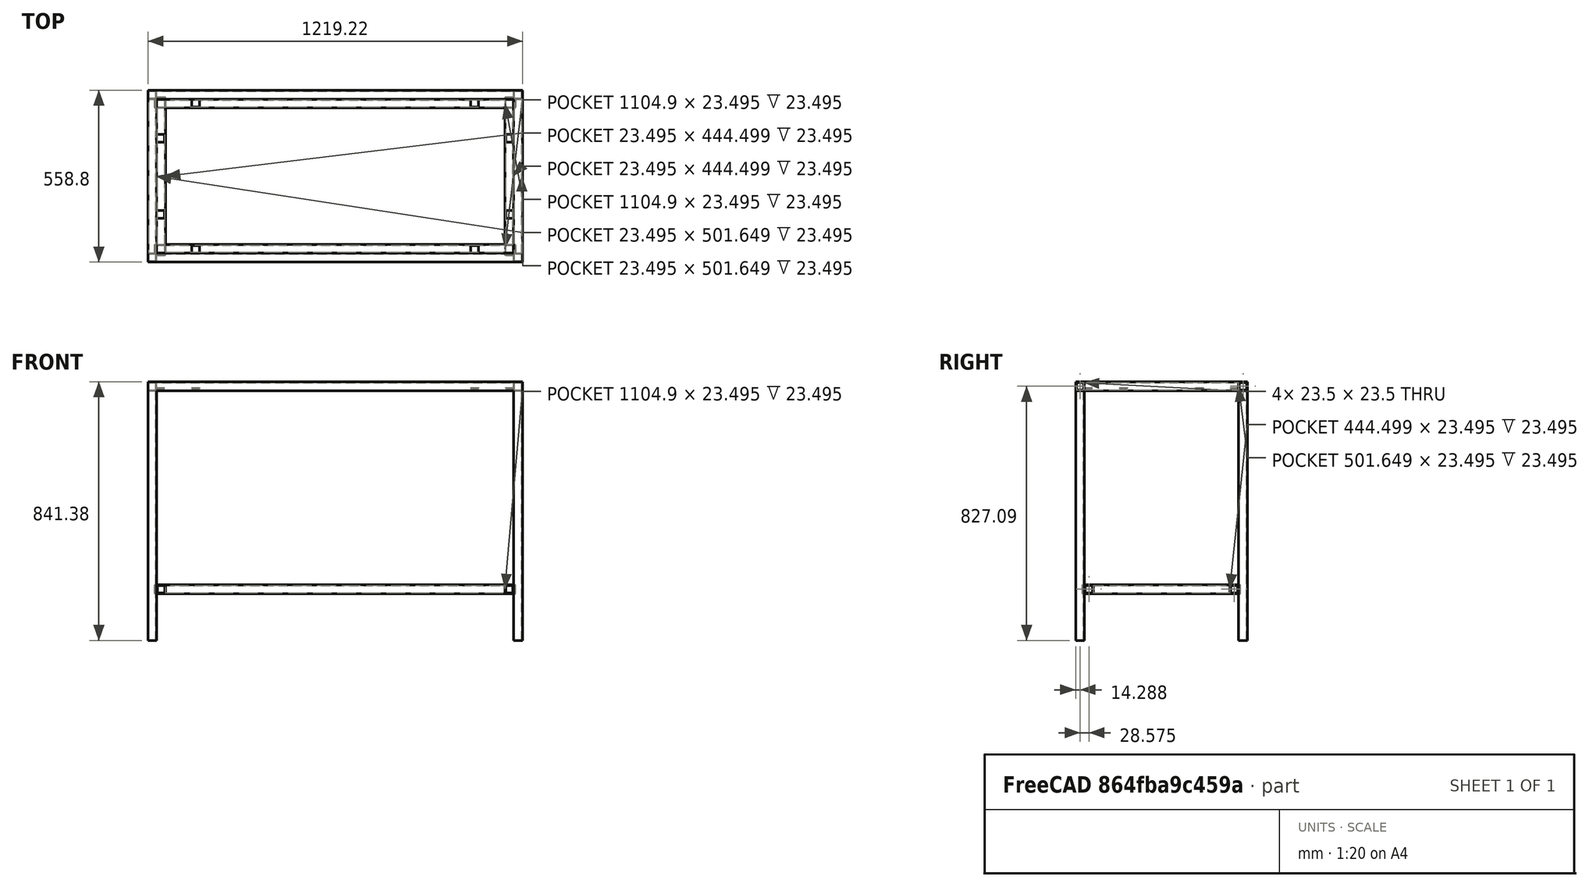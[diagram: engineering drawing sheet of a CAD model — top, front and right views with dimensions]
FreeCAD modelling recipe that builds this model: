
FCSTD DOCUMENT  (FreeCAD 0.21R33668 +26 (Git))
Label: Frame
License: All rights reserved
LicenseURL: http://en.wikipedia.org/wiki/All_rights_reserved
objects: Part::Box×32, Part::Cut×12, Part::MultiFuse×5
note: 49 computed .brp shape members not serialized (recipe doc carries the construction recipe); baked Part::Feature solids carry a one-line shape summary decoded from their .brp

FEATURE [Part::Box] cube
  AttacherType = Attacher::AttachEngine3D
  Height = 28.575
  Length = 1219.21
  Placement = pos=(-609.605,-14.2875,-14.2875) rot=(0,0,1;0rad)
  Width = 28.575
FEATURE [Part::Box] cube001
  AttacherType = Attacher::AttachEngine3D
  Height = 23.495
  Length = 1219.23
  Placement = pos=(-609.615,-11.7475,-11.7475) rot=(0,0,1;0rad)
  Width = 23.495
FEATURE [Part::Cut] difference
  Base = -> cube
  Placement = pos=(0,265.112,0) rot=(0,0,1;0rad)
  Tool = -> cube001
FEATURE [Part::Box] cube002
  AttacherType = Attacher::AttachEngine3D
  Height = 28.575
  Length = 1219.21
  Placement = pos=(-609.605,-14.2875,-14.2875) rot=(0,0,1;0rad)
  Width = 28.575
FEATURE [Part::Box] cube003
  AttacherType = Attacher::AttachEngine3D
  Height = 23.495
  Length = 1219.23
  Placement = pos=(-609.615,-11.7475,-11.7475) rot=(0,0,1;0rad)
  Width = 23.495
FEATURE [Part::Cut] difference001
  Base = -> cube002
  Placement = pos=(0,-265.112,0) rot=(0,0,1;0rad)
  Tool = -> cube003
FEATURE [Part::Box] cube004
  AttacherType = Attacher::AttachEngine3D
  Height = 28.575
  Length = 501.66
  Placement = pos=(-250.83,-14.2875,-14.2875) rot=(0,0,1;0rad)
  Width = 28.575
FEATURE [Part::Box] cube005
  AttacherType = Attacher::AttachEngine3D
  Height = 23.495
  Length = 501.68
  Placement = pos=(-250.84,-11.7475,-11.7475) rot=(0,0,1;0rad)
  Width = 23.495
FEATURE [Part::Cut] difference002
  Base = -> cube004
  Placement = pos=(595.312,0,0) rot=(0,0,1;1.5708rad)
  Tool = -> cube005
FEATURE [Part::Box] cube006
  AttacherType = Attacher::AttachEngine3D
  Height = 28.575
  Length = 501.66
  Placement = pos=(-250.83,-14.2875,-14.2875) rot=(0,0,1;0rad)
  Width = 28.575
FEATURE [Part::Box] cube007
  AttacherType = Attacher::AttachEngine3D
  Height = 23.495
  Length = 501.68
  Placement = pos=(-250.84,-11.7475,-11.7475) rot=(0,0,1;0rad)
  Width = 23.495
FEATURE [Part::Cut] difference003
  Base = -> cube006
  Placement = pos=(-595.312,0,0) rot=(0,0,1;1.5708rad)
  Tool = -> cube007
FEATURE [Part::MultiFuse] Group
  Shapes = -> [difference,difference001,difference002,difference003]
FEATURE [Part::Box] cube008
  AttacherType = Attacher::AttachEngine3D
  Height = 3.175
  Length = 25.4
  Placement = pos=(555.625,-136.525,-7.65175) rot=(0,0,1;0rad)
  Width = 25.4
FEATURE [Part::Box] cube009
  AttacherType = Attacher::AttachEngine3D
  Height = 3.175
  Length = 25.4
  Placement = pos=(555.625,111.125,-7.65175) rot=(0,0,1;0rad)
  Width = 25.4
FEATURE [Part::Box] cube010
  AttacherType = Attacher::AttachEngine3D
  Height = 3.175
  Length = 25.4
  Placement = pos=(-581.025,-136.525,-7.65175) rot=(0,0,1;0rad)
  Width = 25.4
FEATURE [Part::Box] cube011
  AttacherType = Attacher::AttachEngine3D
  Height = 3.175
  Length = 25.4
  Placement = pos=(-581.025,111.125,-7.65175) rot=(0,0,1;0rad)
  Width = 25.4
FEATURE [Part::Box] cube012
  AttacherType = Attacher::AttachEngine3D
  Height = 3.175
  Length = 25.4
  Placement = pos=(-466.725,225.425,-7.65175) rot=(0,0,1;0rad)
  Width = 25.4
FEATURE [Part::Box] cube013
  AttacherType = Attacher::AttachEngine3D
  Height = 3.175
  Length = 25.4
  Placement = pos=(441.325,225.425,-7.65175) rot=(0,0,1;0rad)
  Width = 25.4
FEATURE [Part::Box] cube014
  AttacherType = Attacher::AttachEngine3D
  Height = 3.175
  Length = 25.4
  Placement = pos=(-466.725,-250.825,-7.65175) rot=(0,0,1;0rad)
  Width = 25.4
FEATURE [Part::Box] cube015
  AttacherType = Attacher::AttachEngine3D
  Height = 3.175
  Length = 25.4
  Placement = pos=(441.325,-250.825,-7.65175) rot=(0,0,1;0rad)
  Width = 25.4
FEATURE [Part::MultiFuse] Group001
  Shapes = -> [cube008,cube009,cube010,cube011,cube012,cube013,cube014,cube015]
FEATURE [Part::Box] cube016
  AttacherType = Attacher::AttachEngine3D
  Height = 812.8
  Length = 28.575
  Placement = pos=(-14.2875,-14.2875,-812.8) rot=(0,0,1;0rad)
  Width = 28.575
FEATURE [Part::Box] cube017
  AttacherType = Attacher::AttachEngine3D
  Height = 812.82
  Length = 23.495
  Placement = pos=(-11.7475,-11.7475,-812.81) rot=(0,0,1;0rad)
  Width = 23.495
FEATURE [Part::Cut] difference004
  Base = -> cube016
  Placement = pos=(595.312,265.112,-14.2875) rot=(0,0,1;0rad)
  Tool = -> cube017
FEATURE [Part::Box] cube018
  AttacherType = Attacher::AttachEngine3D
  Height = 812.8
  Length = 28.575
  Placement = pos=(-14.2875,-14.2875,-812.8) rot=(0,0,1;0rad)
  Width = 28.575
FEATURE [Part::Box] cube019
  AttacherType = Attacher::AttachEngine3D
  Height = 812.82
  Length = 23.495
  Placement = pos=(-11.7475,-11.7475,-812.81) rot=(0,0,1;0rad)
  Width = 23.495
FEATURE [Part::Cut] difference005
  Base = -> cube018
  Placement = pos=(-595.312,265.112,-14.2875) rot=(0,0,1;0rad)
  Tool = -> cube019
FEATURE [Part::Box] cube020
  AttacherType = Attacher::AttachEngine3D
  Height = 812.8
  Length = 28.575
  Placement = pos=(-14.2875,-14.2875,-812.8) rot=(0,0,1;0rad)
  Width = 28.575
FEATURE [Part::Box] cube021
  AttacherType = Attacher::AttachEngine3D
  Height = 812.82
  Length = 23.495
  Placement = pos=(-11.7475,-11.7475,-812.81) rot=(0,0,1;0rad)
  Width = 23.495
FEATURE [Part::Cut] difference006
  Base = -> cube020
  Placement = pos=(-595.312,-265.112,-14.2875) rot=(0,0,1;0rad)
  Tool = -> cube021
FEATURE [Part::Box] cube022
  AttacherType = Attacher::AttachEngine3D
  Height = 812.8
  Length = 28.575
  Placement = pos=(-14.2875,-14.2875,-812.8) rot=(0,0,1;0rad)
  Width = 28.575
FEATURE [Part::Box] cube023
  AttacherType = Attacher::AttachEngine3D
  Height = 812.82
  Length = 23.495
  Placement = pos=(-11.7475,-11.7475,-812.81) rot=(0,0,1;0rad)
  Width = 23.495
FEATURE [Part::Cut] difference007
  Base = -> cube022
  Placement = pos=(595.312,-265.112,-14.2875) rot=(0,0,1;0rad)
  Tool = -> cube023
FEATURE [Part::MultiFuse] Group002
  Shapes = -> [difference004,difference005,difference006,difference007]
FEATURE [Part::Box] cube024
  AttacherType = Attacher::AttachEngine3D
  Height = 28.575
  Length = 1174.75
  Placement = pos=(-587.375,-14.2875,-14.2875) rot=(0,0,1;0rad)
  Width = 28.575
FEATURE [Part::Box] cube025
  AttacherType = Attacher::AttachEngine3D
  Height = 23.495
  Length = 1174.77
  Placement = pos=(-587.385,-11.7475,-11.7475) rot=(0,0,1;0rad)
  Width = 23.495
FEATURE [Part::Cut] difference008
  Base = -> cube024
  Placement = pos=(0,236.537,-660.4) rot=(0,0,1;0rad)
  Tool = -> cube025
FEATURE [Part::Box] cube026
  AttacherType = Attacher::AttachEngine3D
  Height = 28.575
  Length = 1174.75
  Placement = pos=(-587.375,-14.2875,-14.2875) rot=(0,0,1;0rad)
  Width = 28.575
FEATURE [Part::Box] cube027
  AttacherType = Attacher::AttachEngine3D
  Height = 23.495
  Length = 1174.77
  Placement = pos=(-587.385,-11.7475,-11.7475) rot=(0,0,1;0rad)
  Width = 23.495
FEATURE [Part::Cut] difference009
  Base = -> cube026
  Placement = pos=(0,-236.537,-660.4) rot=(0,0,1;0rad)
  Tool = -> cube027
FEATURE [Part::Box] cube028
  AttacherType = Attacher::AttachEngine3D
  Height = 28.575
  Length = 514.35
  Placement = pos=(-257.175,-14.2875,-14.2875) rot=(0,0,1;0rad)
  Width = 28.575
FEATURE [Part::Box] cube029
  AttacherType = Attacher::AttachEngine3D
  Height = 23.495
  Length = 514.37
  Placement = pos=(-257.185,-11.7475,-11.7475) rot=(0,0,1;0rad)
  Width = 23.495
FEATURE [Part::Cut] difference010
  Base = -> cube028
  Placement = pos=(566.737,0,-660.4) rot=(0,0,1;1.5708rad)
  Tool = -> cube029
FEATURE [Part::Box] cube030
  AttacherType = Attacher::AttachEngine3D
  Height = 28.575
  Length = 514.35
  Placement = pos=(-257.175,-14.2875,-14.2875) rot=(0,0,1;0rad)
  Width = 28.575
FEATURE [Part::Box] cube031
  AttacherType = Attacher::AttachEngine3D
  Height = 23.495
  Length = 514.37
  Placement = pos=(-257.185,-11.7475,-11.7475) rot=(0,0,1;0rad)
  Width = 23.495
FEATURE [Part::Cut] difference011
  Base = -> cube030
  Placement = pos=(-566.737,0,-660.4) rot=(0,0,1;1.5708rad)
  Tool = -> cube031
FEATURE [Part::MultiFuse] Group003
  Shapes = -> [difference008,difference009,difference010,difference011]
FEATURE [Part::MultiFuse] union
  Shapes = -> [Group,Group001,Group002,Group003]
